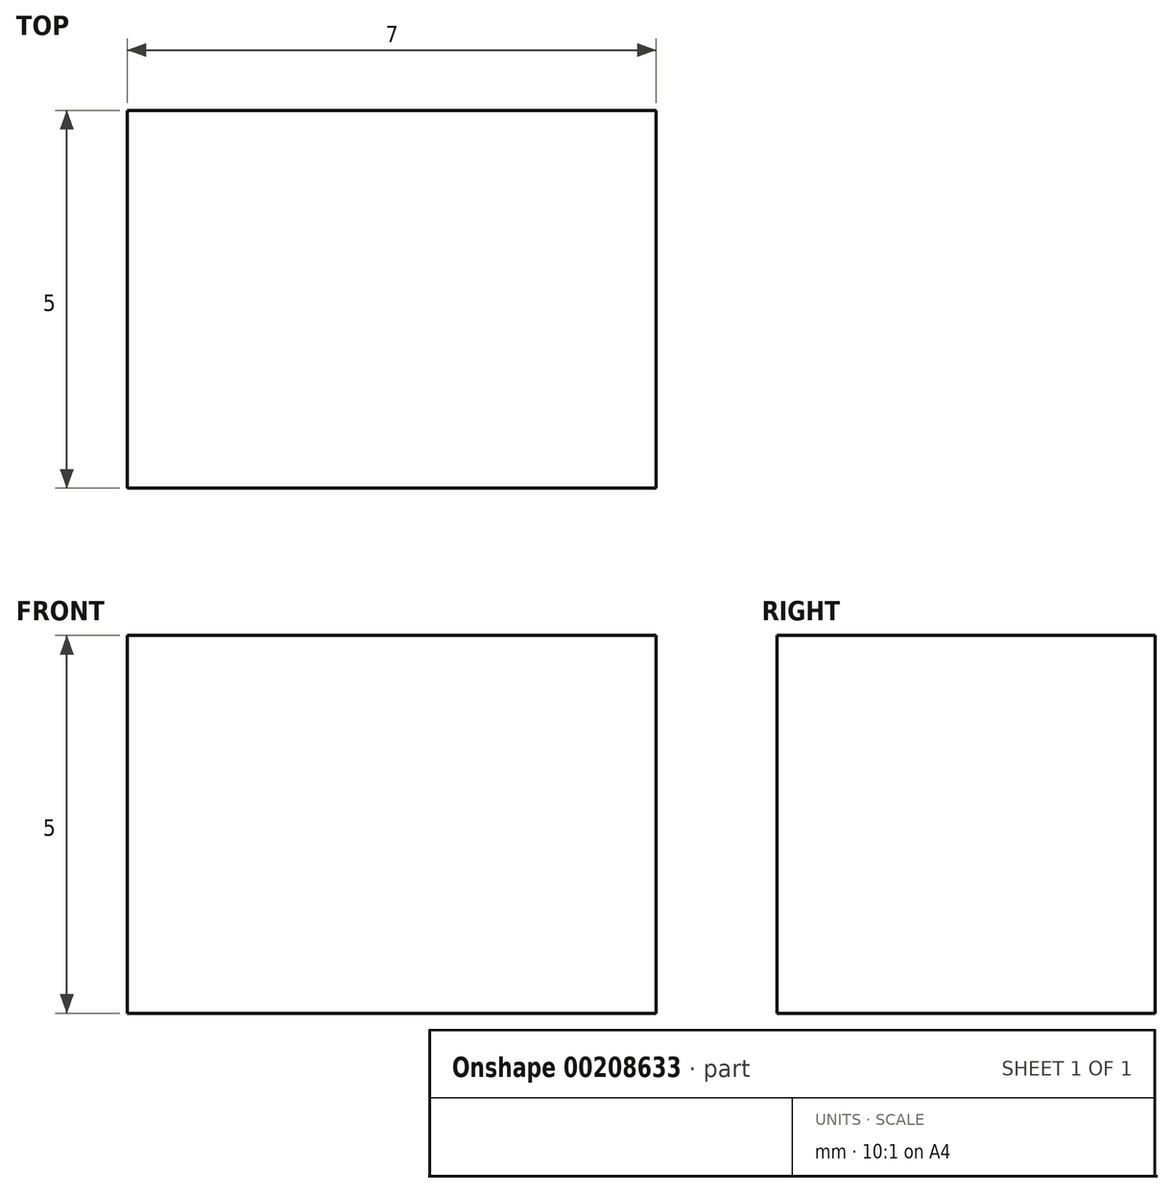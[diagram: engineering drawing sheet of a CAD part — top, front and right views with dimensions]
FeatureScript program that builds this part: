
annotation { "Feature Type Name" : "Feature", "Feature Type Description" : "" }
export const myFeature = defineFeature(function(context is Context, id is Id, definition is map)
    precondition{}
    {
        {
            var Q0;
            Q0=qCreatedBy(makeId("Front.planeOp"),FACE);
            var sketch = newSketch(context, id + "F1", { "sketchPlane" : qUnion([Q0])});
            skLineSegment(sketch, "E0.bottom", {"start": v(-7, -5) * mm, "end": v(0, -5) * mm});
            skLineSegment(sketch, "E0.top", {"start": v(-7, 0) * mm, "end": v(0, 0) * mm});
            skLineSegment(sketch, "E0.left", {"start": v(-7, -5) * mm, "end": v(-7, 0) * mm});
            skLineSegment(sketch, "E0.right", {"start": v(0, -5) * mm, "end": v(0, 0) * mm});
            skSolve(sketch);
        }
        {
            var Q0;
            Q0 = qSketchRegion(id + "F1", true);
            extrude(context, id + "F0", {"entities" : qUnion([Q0]), "depth" : 5 * mm});
        }
    });
